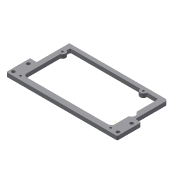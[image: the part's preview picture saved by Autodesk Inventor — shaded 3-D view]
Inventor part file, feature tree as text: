
AUTODESK INVENTOR PART (.ipt)
format: ipt  version: 2017 (Build 210142000, 142)  size: 1,086,464 bytes
history: native  units: mm
features: sketch x10, fillet x9, extrude x7, projected_geometry x3, other x3, hole x2, reference x1
ambient origin geometry x8: Origin, YZ Plane, XZ Plane, XY Plane, X Axis, Y Axis, Z Axis, Center Point
bodies: Solid1 (feature_tree)
feature tree (35):
  extrude  "Extrusion1"  TaperAngle=90.0deg  [1 undecoded]
  extrude  "Extrusion2"  Depth=2.0mm
  fillet  "Fillet1"  Radius=2.0mm
  fillet  "Fillet2"  Radius=2.0mm
  fillet  "Fillet3"  Radius=2.0mm
  fillet  "Fillet4"  Radius=2.0mm
  fillet  "Fillet5"  [1 undecoded]
  extrude  "Extrusion3"  Depth=10.0mm TaperAngle=0.0deg
  fillet  "Fillet6"  Radius=2.0mm
  extrude  "Extrusion4"  Depth=2.0mm
  fillet  "Fillet7"  Radius=10.0mm
  hole  "Hole1"  [1 undecoded]
  hole  "Hole2"  [1 undecoded]
  extrude  "Extrusion5"  [1 undecoded]
  fillet  "Fillet8"  [1 undecoded]
  sketch  "Sketch9"  dims[d39=6.0mm d40=0.0mm d41=2.0mm]
  extrude  "Extrusion6"  [1 undecoded]
  extrude  "Extrusion7"  [1 undecoded]
  fillet  "Fillet9"  [1 undecoded]
  sketch  "Sketch1"  dims[d0=6.0mm d1=0.0mm d3=90.0deg]
  sketch  "Sketch2"  dims[d5=6.0mm d6=0.0mm d7=2.0mm d8=2.0mm d9=2.0mm d10=2.0mm d11=2.0mm d12=90.0deg]
  sketch  "Sketch3"  dims[d13=90.0deg d14=10.0mm d15=0.0mm d16=2.0mm]
  sketch  "Sketch4"  dims[d17=10.0mm d18=0.0mm d19=2.0mm]
  sketch  "Sketch5"  dims[d20=3.3mm d21=6.0mm d22=4.0mm d23=2.0mm d24=90.0deg d25=8.0mm d26=20.594885mm]
  projected_geometry  "Projected Loop2"
  sketch  "Sketch6"  dims[d27=5.4mm d28=6.0mm d29=4.0mm d30=2.0mm d31=90.0deg d32=8.0mm d33=20.594885mm d34=10.0mm d35=0.0mm]
  projected_geometry  "Projected Loop3"
  sketch  "Sketch7"  dims[d36=4.0mm d37=6.0mm d38=0.0mm]
  projected_geometry  "Projected Loop4"
  sketch  "Sketch10"
  sketch  "Sketch11"
  reference  "Reference3"
  parser-record x1  (decoder bookkeeping rows leaked as tree rows — omitted from the tree; the rows remain in map.json)
  other  "PSU.iam"
  other  "power supply:1"
note: 9 required parameter values undecoded (feature->parameter linkage not recoverable at this tier; creation-order binding heuristic only, values carry confidence <= 0.55)
note: 1 file-system path scrubbed to <path> (originals preserved in map.json)
